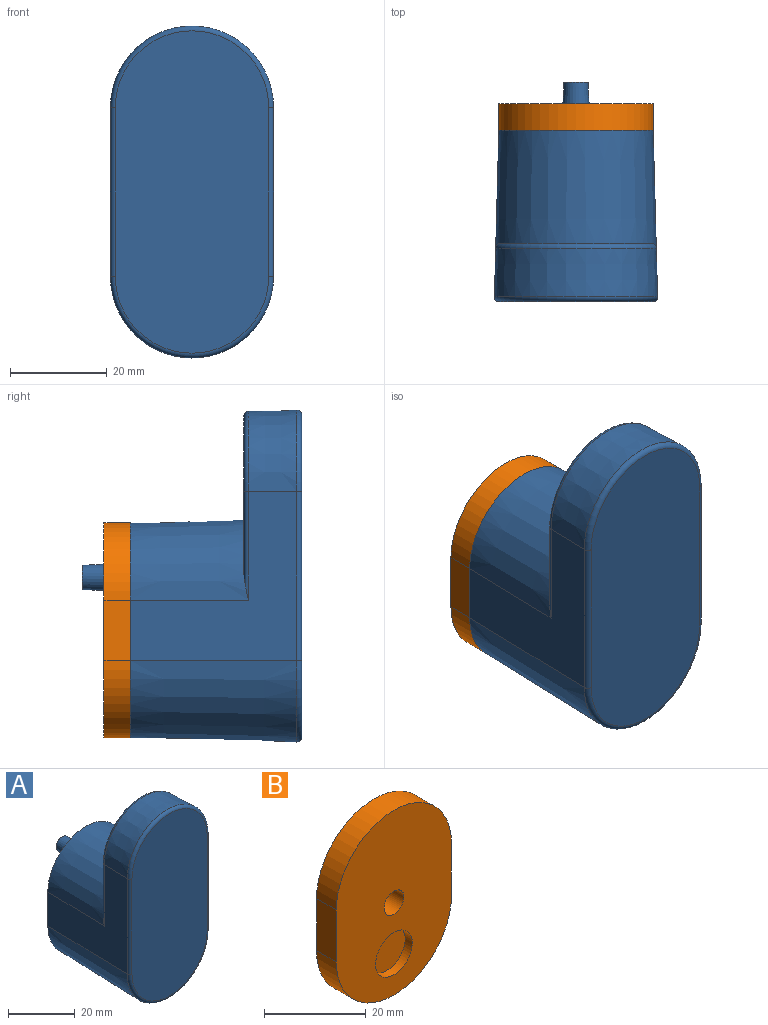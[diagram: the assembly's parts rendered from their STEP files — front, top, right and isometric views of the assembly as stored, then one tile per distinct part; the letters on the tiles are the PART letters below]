
ASSEMBLY  parts=2 mates=1
PART A: 24 faces, bbox 36.6x45.5x71.6 mm
  f0: cone r=16mm half-angle=1.5deg, axis (0,-1,0), area 527.1mm2, adj f1,f3,f12,f17
  f1: plane 35x34.47mm, normal (-1,0.03,0), area 656.1mm2, adj f0,f2,f6,f7,f13,f16
  f2: cone r=16mm half-angle=1.5deg, axis (0,-1,0), area 1782.3mm2, adj f1,f3,f7,f15
  f3: plane 35x34.47mm, normal (1,0.03,0), area 656.1mm2, adj f0,f2,f6,f7,f14,f18
  f4: plane 66.81x31.81mm, normal (0,-1,0), area 1907.7mm2, adj f12,f13,f14,f15
  f5: plane 32.54x31.28mm, normal (0,1,0), area 661.8mm2, adj f6,f16,f17,f18
  f6: cone r=16mm half-angle=1.5deg, axis (0,-1,0), area 1208.7mm2, adj f1,f3,f5,f7,f16,f18
  f7: plane 44.5x32mm, normal (0,1,0), area 1053.6mm2, adj f1,f2,f3,f6,f8,f19,f22
  f8: cone r=5mm half-angle=3deg, axis (0,-1,0), area 25.1mm2, adj f7,f21
  f9: plane 7.92x7.92mm, normal (0,1,0), area 49.2mm2, adj f21
  f10: cone r=2.75mm half-angle=2deg, axis (0,1,0), area 34.9mm2, adj f19,f20
  f11: plane 3.29x3.29mm, normal (0,1,0), area 8.5mm2, adj f20
  f12: torus R=15.9mm, axis (0,-1,0), area 83mm2, adj f0,f4,f13,f14
  f13: cylinder r=1mm len=35mm, axis (0,0,-1), area 55.9mm2, adj f1,f4,f12,f15
  f14: cylinder r=1mm len=35mm, axis (0,0,-1), area 55.9mm2, adj f3,f4,f12,f15
  f15: torus R=15.9mm, axis (0,-1,0), area 83mm2, adj f2,f4,f13,f14
  f16: cylinder r=1mm len=22.5mm, axis (0,0,1), area 30.4mm2, adj f1,f5,f6,f17
  f17: torus R=15.64mm, axis (0,-1,0), area 79mm2, adj f0,f5,f16,f18
  f18: cylinder r=1mm len=22.5mm, axis (0,0,1), area 30.4mm2, adj f3,f5,f6,f17
  f19: torus R=3.72mm, axis (0,1,0), area 29.8mm2, adj f7,f10
  f20: torus R=1.64mm, axis (0,1,0), area 21.9mm2, adj f10,f11
  f21: torus R=3.96mm, axis (0,1,0), area 43.7mm2, adj f8,f9
  f22: cone r=2.5mm half-angle=3deg, axis (0,-1,0), area 173.8mm2, adj f7,f23
  f23: plane 5x5mm, normal (0,1,0), area 19.6mm2, adj f22
PART B: 9 faces, bbox 32x5.5x44.5 mm
  f0: plane 12.5x5.5mm, normal (1,0,0), area 68.8mm2, adj f1,f3,f4,f5
  f1: cylinder r=16mm len=32mm, axis (0,1,0), area 276.5mm2, adj f0,f2,f4,f5
  f2: plane 12.5x5.5mm, normal (-1,0,0), area 68.8mm2, adj f1,f3,f4,f5
  f3: cylinder r=16mm len=32mm, axis (0,1,0), area 276.5mm2, adj f0,f2,f4,f5
  f4: plane 44.5x32mm, normal (0,-1,0), area 1098.8mm2, adj f0,f1,f2,f3,f6,f8
  f5: plane 44.5x32mm, normal (0,1,0), area 1180.5mm2, adj f0,f1,f2,f3,f8
  f6: cylinder r=5.1mm len=10.2mm, axis (0,-1,0), area 64.1mm2, adj f4,f7
  f7: plane 10.2x10.2mm, normal (0,-1,0), area 81.7mm2, adj f6
  f8: cylinder r=2.75mm len=5.5mm, axis (0,-1,0), area 95mm2, adj f4,f5
PLACE A t=(0,-29.5,21)mm
PLACE B t=(0,-0.5,18.5)mm
MATE fastened A.f10 <-> B.f8  axis (0,1,0) through (0,-6,12.25)mm
